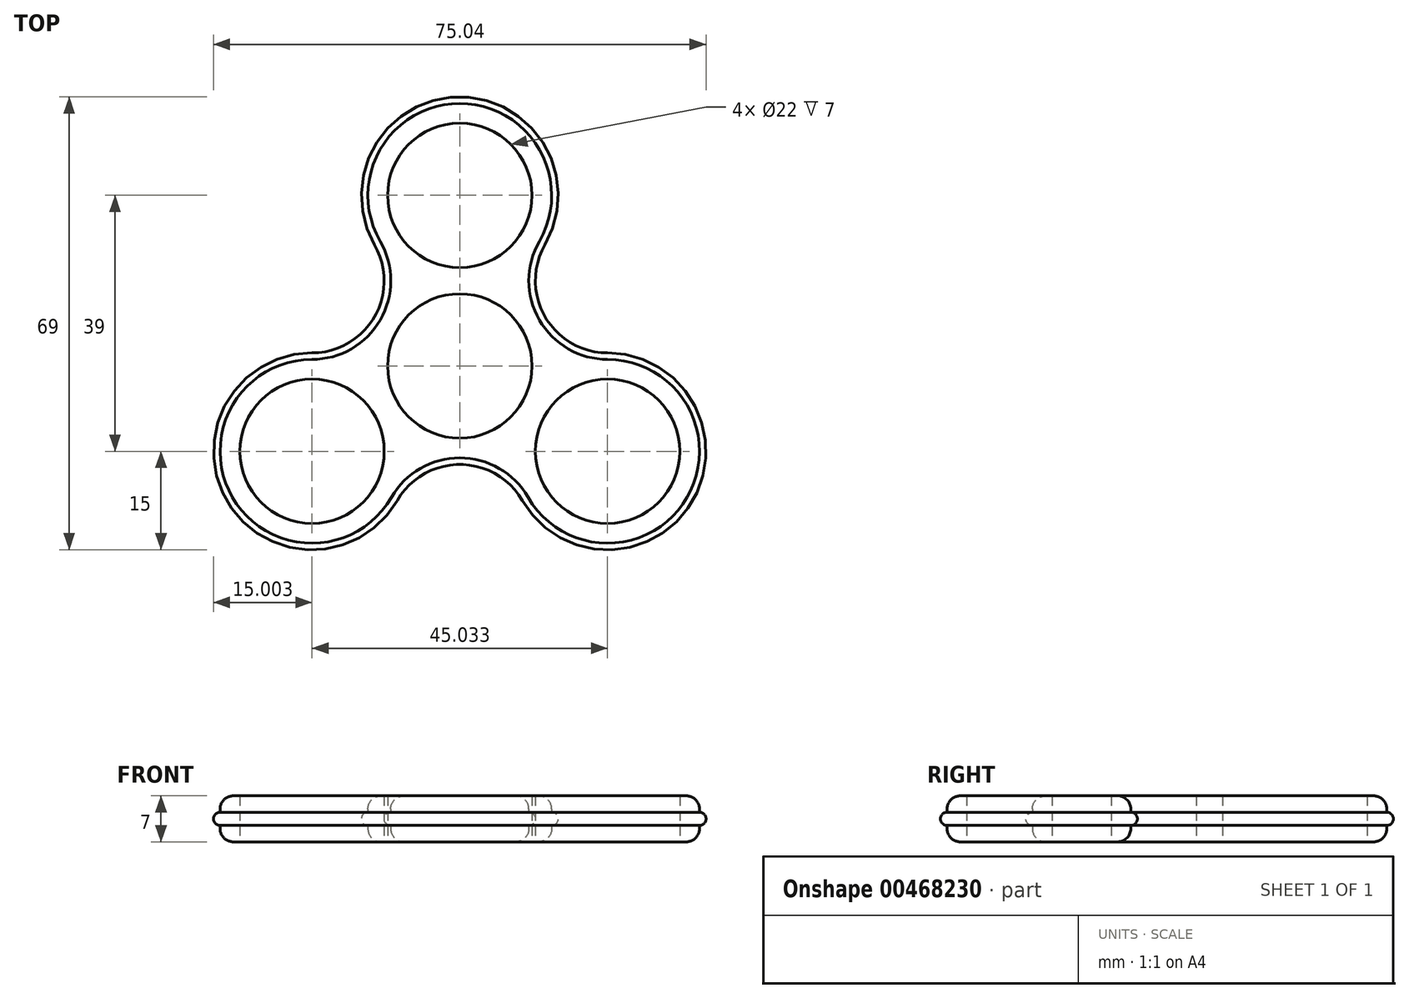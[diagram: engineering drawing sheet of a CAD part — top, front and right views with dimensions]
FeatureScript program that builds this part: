
annotation { "Feature Type Name" : "Feature", "Feature Type Description" : "" }
export const myFeature = defineFeature(function(context is Context, id is Id, definition is map)
    precondition{}
    {
        {
            var Q0;
            Q0=qCreatedBy(makeId("Top.planeOp"),FACE);
            var sketch = newSketch(context, id + "F0", { "sketchPlane" : qUnion([Q0])});
            skCircle(sketch, "E0", {"center": v(0, 0) * mm, "radius": 11 * mm});
            skCircle(sketch, "E1", {"center": v(0, 26) * mm, "radius": 11 * mm});
            skArc(sketch, "E2.0", {"start": v(12.12, 19) * mm, "mid": v(0, 40) * mm, "end": v(-12.12, 19) * mm});
            skCircle(sketch, "E3.1.0", {"center": v(-22.52, -13) * mm, "radius": 11 * mm});
            skArc(sketch, "E3.1.1", {"start": v(-22.52, 1) * mm, "mid": v(-34.64, -20) * mm, "end": v(-10.4, -20) * mm});
            skCircle(sketch, "E3.2.0", {"center": v(22.52, -13) * mm, "radius": 11 * mm});
            skArc(sketch, "E3.2.1", {"start": v(10.4, -20) * mm, "mid": v(34.64, -20) * mm, "end": v(22.52, 1) * mm});
            skArc(sketch, "E4", {"start": v(-12.12, 19) * mm, "mid": v(-12.12, 7) * mm, "end": v(-22.52, 1) * mm});
            skArc(sketch, "E5", {"start": v(12.12, 19) * mm, "mid": v(12.12, 7) * mm, "end": v(22.52, 1) * mm});
            skArc(sketch, "E6", {"start": v(-10.4, -20) * mm, "mid": v(0, -14) * mm, "end": v(10.4, -20) * mm});
            skLineSegment(sketch, "E7", {"start": v(0, 0) * mm, "end": v(12.12, 7) * mm});
            skPoint(sketch, "E8", {"position": v(0, 40) * mm});
            skSolve(sketch);
        }
        {
            var Q0;
            Q0=qCreatedBy(makeId("Right.planeOp"),FACE);
            var sketch = newSketch(context, id + "F1", { "sketchPlane" : qUnion([Q0])});
            skCircle(sketch, "E9", {"center": v(40, 0) * mm, "radius": 1 * mm});
            skSolve(sketch);
        }
        {
            var Q0;
            Q0=makeQuery(id+"F0.imprint","IMPRINT",FACE,{"disambiguationData":[TD([[makeQuery(id+"F0.imprint","IMPRINT",EDGE,{"derivedFrom":sQuery(id+"F0.wireOp",EDGE,"E0")}),-1.0]])]});
            extrude(context, id + "F2", {"entities" : qUnion([Q0]), "endBound" : BoundingType.SYMMETRIC, "depth" : 7 * mm});
        }
        {
            var Q0;
            Q0=qCreatedBy(makeId("Top.planeOp"),FACE);
            var sketch = newSketch(context, id + "F3", { "sketchPlane" : qUnion([Q0])});
            skArc(sketch, "E10.0", {"start": v(0, 40) * mm, "mid": v(-12.12, 33) * mm, "end": v(-12.12, 19) * mm});
            skArc(sketch, "E11.1.0", {"start": v(-22.52, 1) * mm, "mid": v(-34.64, -20) * mm, "end": v(-10.4, -20) * mm});
            skPoint(sketch, "E11.center", {"position": v(0, 0) * mm});
            skArc(sketch, "E12", {"start": v(-12.12, 19) * mm, "mid": v(-12.12, 7) * mm, "end": v(-22.52, 1) * mm});
            skArc(sketch, "E13", {"start": v(0, -14) * mm, "mid": v(-6, -15.6) * mm, "end": v(-10.4, -20) * mm});
            skPoint(sketch, "E14", {"position": v(0, 40) * mm});
            skPoint(sketch, "E15", {"position": v(0, -14) * mm});
            skPoint(sketch, "E16.start.orphan", {"position": v(12.12, 19) * mm});
            skSolve(sketch);
        }
        {
            var Q0;
            Q0=qCreatedBy(makeId("Top.planeOp"),FACE);
            var sketch = newSketch(context, id + "F4", { "sketchPlane" : qUnion([Q0])});
            skArc(sketch, "E17.0", {"start": v(12.12, 19) * mm, "mid": v(12.12, 33) * mm, "end": v(0, 40) * mm});
            skArc(sketch, "E18.2.0", {"start": v(10.4, -20) * mm, "mid": v(34.64, -20) * mm, "end": v(22.52, 1) * mm});
            skPoint(sketch, "E18.center", {"position": v(0, 0) * mm});
            skArc(sketch, "E19", {"start": v(12.12, 19) * mm, "mid": v(12.12, 7) * mm, "end": v(22.52, 1) * mm});
            skArc(sketch, "E20", {"start": v(10.4, -20) * mm, "mid": v(6, -15.6) * mm, "end": v(0, -14) * mm});
            skPoint(sketch, "E21", {"position": v(0, -14) * mm});
            skPoint(sketch, "E22", {"position": v(0, 40) * mm});
            skPoint(sketch, "E23.orphan", {"position": v(-12.12, 19) * mm});
            skSolve(sketch);
        }
        {
            var Q0;
            Q0=makeQuery(id+"F1.imprint","IMPRINT",FACE,{"disambiguationData":[TD([[makeQuery(id+"F1.imprint","IMPRINT",EDGE,{"derivedFrom":sQuery(id+"F1.wireOp",EDGE,"E9")}),1.0]])]});
            var Q1;
            Q1 = qConstructionFilter(qBodyType(qCreatedBy(id + "F3" ,EDGE), BodyType.WIRE), ConstructionObject.NO);
            var Q2;
            Q2 = qConstructionFilter(qBodyType(qCreatedBy(id + "F4" ,EDGE), BodyType.WIRE), ConstructionObject.NO);
            sweep(context, id + "F5", {"operationType" : NewBodyOperationType.ADD, "profiles" : qUnion([Q0]), "path" : qUnion([Q1, Q2])});
        }
        {
            var Q0;
            Q0=makeQuery(id+"F2.opExtrude","CAP_EDGE",EDGE,{"disambiguationData":[OSD([sQuery(id+"F0.wireOp",EDGE,"E2.0")])],"isStart":false});
            var Q1;
            Q1=makeQuery(id+"F2.opExtrude","CAP_EDGE",EDGE,{"disambiguationData":[OSD([sQuery(id+"F0.wireOp",EDGE,"E4")])],"isStart":false});
            var Q2;
            Q2=makeQuery(id+"F2.opExtrude","CAP_EDGE",EDGE,{"disambiguationData":[OSD([sQuery(id+"F0.wireOp",EDGE,"E3.1.1")])],"isStart":false});
            var Q3;
            Q3=makeQuery(id+"F2.opExtrude","CAP_EDGE",EDGE,{"disambiguationData":[OSD([sQuery(id+"F0.wireOp",EDGE,"E6")])],"isStart":false});
            var Q4;
            Q4=makeQuery(id+"F2.opExtrude","CAP_EDGE",EDGE,{"disambiguationData":[OSD([sQuery(id+"F0.wireOp",EDGE,"E3.2.1")])],"isStart":false});
            var Q5;
            Q5=makeQuery(id+"F2.opExtrude","CAP_EDGE",EDGE,{"disambiguationData":[OSD([sQuery(id+"F0.wireOp",EDGE,"E5")])],"isStart":false});
            var Q6;
            Q6=makeQuery(id+"F2.opExtrude","CAP_EDGE",EDGE,{"disambiguationData":[OSD([sQuery(id+"F0.wireOp",EDGE,"E3.1.1")])],"isStart":true});
            var Q7;
            Q7=makeQuery(id+"F2.opExtrude","CAP_EDGE",EDGE,{"disambiguationData":[OSD([sQuery(id+"F0.wireOp",EDGE,"E4")])],"isStart":true});
            var Q8;
            Q8=makeQuery(id+"F2.opExtrude","CAP_EDGE",EDGE,{"disambiguationData":[OSD([sQuery(id+"F0.wireOp",EDGE,"E2.0")])],"isStart":true});
            var Q9;
            Q9=makeQuery(id+"F2.opExtrude","CAP_EDGE",EDGE,{"disambiguationData":[OSD([sQuery(id+"F0.wireOp",EDGE,"E5")])],"isStart":true});
            var Q10;
            Q10=makeQuery(id+"F2.opExtrude","CAP_EDGE",EDGE,{"disambiguationData":[OSD([sQuery(id+"F0.wireOp",EDGE,"E3.2.1")])],"isStart":true});
            fillet(context, id + "F6", {"entities" : qUnion([Q0, Q1, Q2, Q3, Q4, Q5, Q6, Q7, Q8, Q9, Q10]), "radius" : 2 * mm, "tangentPropagation" : true, "allowEdgeOverflow" : false});
        }
    });
